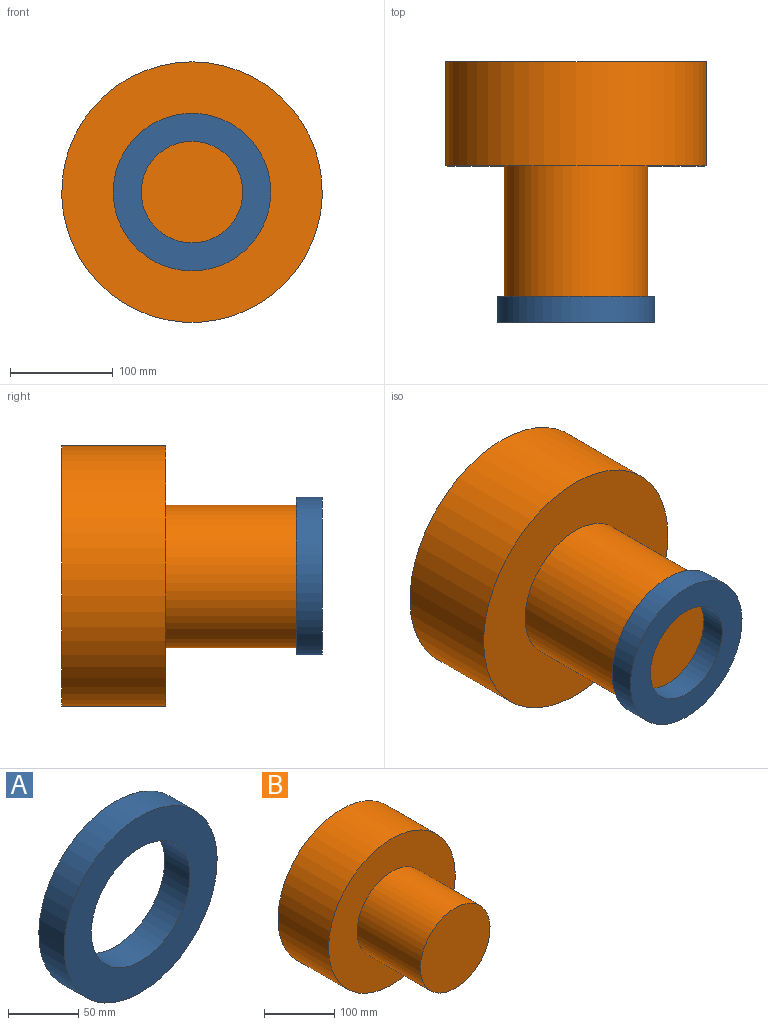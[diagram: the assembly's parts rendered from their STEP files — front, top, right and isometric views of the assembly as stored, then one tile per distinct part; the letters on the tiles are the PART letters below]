
ASSEMBLY  parts=2 mates=1
PART A: 4 faces, bbox 153.7x25.4x153.7 mm
  f0: cylinder r=49.54mm len=99.09mm, axis (0,1,0), area 7906.7mm2, adj f2,f3
  f1: cylinder r=76.83mm len=153.66mm, axis (0,1,0), area 12261.6mm2, adj f2,f3
  f2: plane 153.66x153.66mm, normal (0,-1,0), area 10833.5mm2, adj f0,f1
  f3: plane 153.66x153.66mm, normal (0,1,0), area 10833.5mm2, adj f0,f1
PART B: 5 faces, bbox 254x228.6x254 mm
  f0: plane 254x254mm, normal (0,-1,0), area 35342.8mm2, adj f2,f4
  f1: plane 254x254mm, normal (0,1,0), area 50670.7mm2, adj f4
  f2: cylinder r=69.85mm len=139.7mm, axis (0,1,0), area 55737.8mm2, adj f0,f3
  f3: plane 139.7x139.7mm, normal (0,-1,0), area 15327.9mm2, adj f2
  f4: cylinder r=127mm len=254mm, axis (0,1,0), area 81073.2mm2, adj f0,f1
PLACE A t=(-53.02,-107.33,56.36)mm
PLACE B t=(-53.02,-107.33,56.36)mm
MATE fastened A.f0 <-> B.f2  axis (0,1,0) through (-53.02,-107.33,56.36)mm
